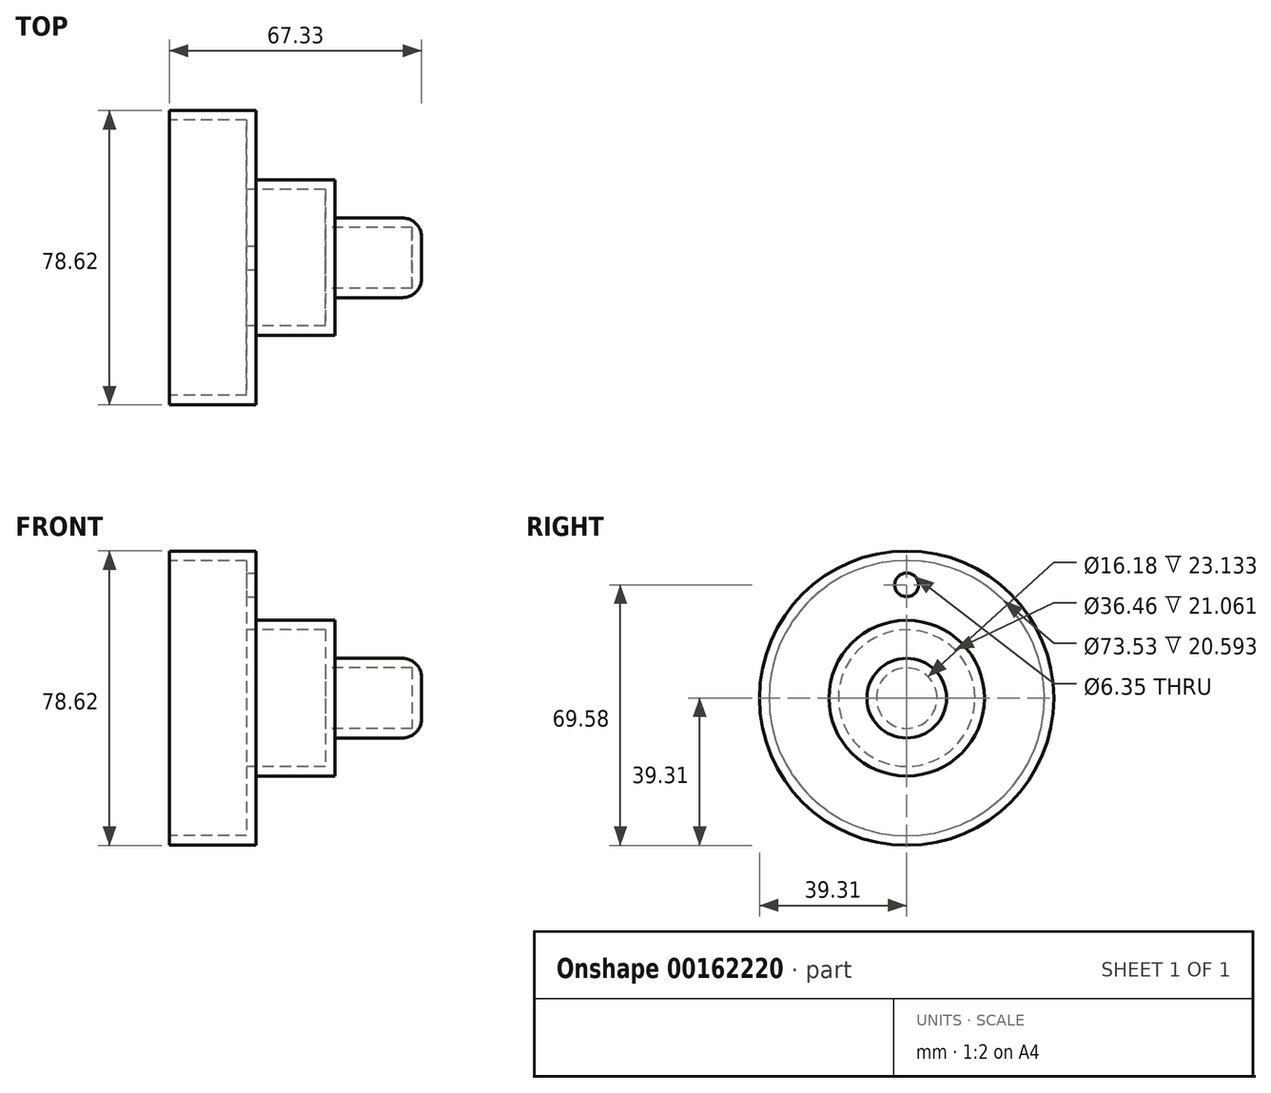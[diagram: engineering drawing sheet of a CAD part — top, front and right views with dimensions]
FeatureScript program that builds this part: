
annotation { "Feature Type Name" : "Feature", "Feature Type Description" : "" }
export const myFeature = defineFeature(function(context is Context, id is Id, definition is map)
    precondition{}
    {
        {
            var Q0;
            Q0=qCreatedBy(makeId("Front.planeOp"),FACE);
            var sketch = newSketch(context, id + "F0", { "sketchPlane" : qUnion([Q0])});
            skLineSegment(sketch, "E0", {"start": v(0, 0) * mm, "end": v(67.33, 0) * mm});
            skLineSegment(sketch, "E1", {"start": v(67.33, 0) * mm, "end": v(67.33, 10.63) * mm});
            skLineSegment(sketch, "E2", {"start": v(67.33, 10.63) * mm, "end": v(44.2, 10.63) * mm});
            skLineSegment(sketch, "E3", {"start": v(44.2, 10.63) * mm, "end": v(44.2, 20.77) * mm});
            skLineSegment(sketch, "E4", {"start": v(44.2, 20.77) * mm, "end": v(23.13, 20.77) * mm});
            skLineSegment(sketch, "E5", {"start": v(23.13, 20.77) * mm, "end": v(23.13, 39.3) * mm});
            skLineSegment(sketch, "E6", {"start": v(23.13, 39.3) * mm, "end": v(0, 39.3) * mm});
            skLineSegment(sketch, "E7", {"start": v(0, 39.3) * mm, "end": v(0, 0) * mm});
            skSolve(sketch);
        }
        {
            var Q0;
            Q0=makeQuery(id+"F0.imprint","IMPRINT",FACE,{"disambiguationData":[TD([[makeQuery(id+"F0.imprint","IMPRINT",EDGE,{"derivedFrom":sQuery(id+"F0.wireOp",EDGE,"E0")}),1.0]])]});
            var Q1;
            Q1=sQuery(id+"F0.wireOp",EDGE,"E0");
            revolve(context, id + "F1", {"entities" : qUnion([Q0]), "axis" : qUnion([Q1]), "revolveType" : RevolveType.FULL});
        }
        {
            var Q0;
            Q0=makeQuery(id+"F1.opRevolve","SWEPT_FACE",FACE,{"disambiguationData":[OSD([sQuery(id+"F0.wireOp",EDGE,"E7")])]});
            shell(context, id + "F2", {"entities" : qUnion([Q0]), "thickness" : 2.54 * mm});
        }
        {
            var Q0;
            Q0=makeQuery(id+"F1.opRevolve","SWEPT_EDGE",EDGE,{"disambiguationData":[OSD([sQuery(id+"F0.wireOp",EDGE,"E1"),sQuery(id+"F0.wireOp",EDGE,"E2")])]});
            fillet(context, id + "F3", {"entities" : qUnion([Q0]), "radius" : 5.08 * mm, "tangentPropagation" : true, "allowEdgeOverflow" : false});
        }
        {
            var Q0;
            Q0=makeQuery(id+"F1.opRevolve","SWEPT_FACE",FACE,{"disambiguationData":[OSD([sQuery(id+"F0.wireOp",EDGE,"E5")])]});
            var sketch = newSketch(context, id + "F4", { "sketchPlane" : qUnion([Q0])});
            skPoint(sketch, "E8", {"position": v(0, 30.27) * mm});
            skSolve(sketch);
        }
        {
            var Q0;
            Q0=sQuery(id+"F4.wireOp",VERTEX,"E8");
            var Q1;
            Q1=makeQuery(id+"F1.opRevolve","SWEPT_BODY",BODY,{"disambiguationData":[OSD([sQuery(id+"F0.wireOp",EDGE,"E0"),sQuery(id+"F0.wireOp",EDGE,"E1"),sQuery(id+"F0.wireOp",EDGE,"E2"),sQuery(id+"F0.wireOp",EDGE,"E3"),sQuery(id+"F0.wireOp",EDGE,"E4"),sQuery(id+"F0.wireOp",EDGE,"E5"),sQuery(id+"F0.wireOp",EDGE,"E6"),sQuery(id+"F0.wireOp",EDGE,"E7")])]});
            hole(context, id + "F5", {"style" : HoleStyle.SIMPLE, "endStyle" : HoleEndStyle.THROUGH, "holeDiameter" : 6.35 * mm, "tappedDepth" : 12.7 * mm, "tapClearance" : 3, "locations" : qUnion([Q0]), "scope" : qUnion([Q1])});
        }
    });
